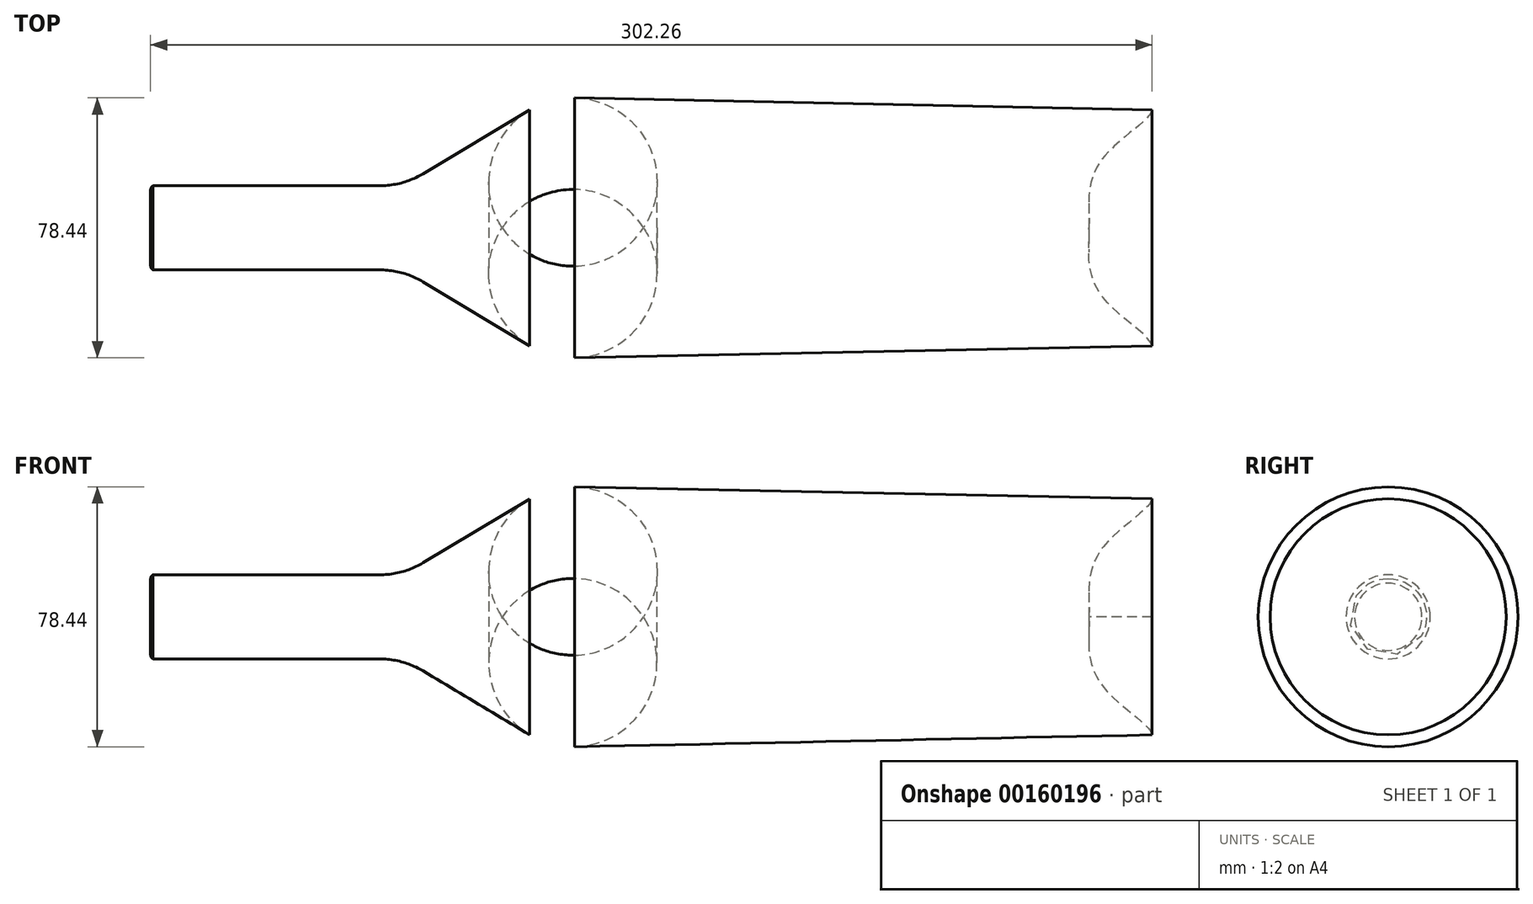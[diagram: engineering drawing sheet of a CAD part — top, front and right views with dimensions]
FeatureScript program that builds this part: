
annotation { "Feature Type Name" : "Feature", "Feature Type Description" : "" }
export const myFeature = defineFeature(function(context is Context, id is Id, definition is map)
    precondition{}
    {
        {
            var Q0;
            Q0=qCreatedBy(makeId("Top.planeOp"),FACE);
            var sketch = newSketch(context, id + "F0", { "sketchPlane" : qUnion([Q0])});
            skLineSegment(sketch, "E0", {"start": v(-285.75, -12.7) * mm, "end": v(-216.59, -12.7) * mm});
            skLineSegment(sketch, "E1", {"start": v(-203.52, -16.32) * mm, "end": v(-171.38, -35.6) * mm});
            skLineSegment(sketch, "E2", {"start": v(-157.78, -39.22) * mm, "end": v(19.05, -35.56) * mm});
            skLineSegment(sketch, "E3", {"start": v(0, 0) * mm, "end": v(-285.75, 0) * mm});
            skLineSegment(sketch, "E4", {"start": v(-285.75, 0) * mm, "end": v(-285.75, -12.7) * mm});
            skPoint(sketch, "E5.visualSharp", {"position": v(-209.55, -12.7) * mm});
            skArc(sketch, "E5.filletArc", {"start": v(-203.52, -16.32) * mm, "mid": v(-209.8, -13.62) * mm, "end": v(-216.59, -12.7) * mm});
            skPoint(sketch, "E6.visualSharp", {"position": v(-165.1, -39.37) * mm});
            skArc(sketch, "E6.filletArc", {"start": v(-171.38, -35.6) * mm, "mid": v(-164.83, -38.37) * mm, "end": v(-157.78, -39.22) * mm});
            skFitSpline(sketch, "E7", {"points": [v(19.05, -35.56) * mm, v(3.02, -18.55) * mm, v(0, -4.3) * mm, v(0, 0) * mm], "startDerivative": vector(-1.53, 31.94) * mm, "endDerivative": vector(0, 30.48) * mm});
            skFitSpline(sketch, "E8.0", {"points": [v(16.51, -35.68) * mm, v(16.5, -35.62) * mm, v(16.48, -35.41) * mm, v(16.22, -34.84) * mm, v(15.69, -34.06) * mm, v(14.9, -33.15) * mm, v(13.88, -32.16) * mm, v(12.3, -30.74) * mm, v(9.97, -28.83) * mm, v(7.45, -26.76) * mm, v(5.46, -25) * mm, v(4, -23.64) * mm, v(2.64, -22.2) * mm, v(1.6, -20.94) * mm, v(0.84, -19.87) * mm, v(0.15, -18.79) * mm, v(-0.58, -17.42) * mm, v(-1.27, -15.78) * mm, v(-1.96, -13.61) * mm, v(-2.45, -11) * mm, v(-2.61, -8.64) * mm, v(-2.63, -6.96) * mm, v(-2.6, -5.83) * mm, v(-2.57, -5) * mm, v(-2.55, -4.44) * mm, v(-2.53, -4.06) * mm, v(-2.52, -3.72) * mm, v(-2.52, -3.3) * mm, v(-2.51, -2.83) * mm, v(-2.52, -2.26) * mm, v(-2.53, -1.43) * mm, v(-2.54, -0.65) * mm, v(-2.54, 0) * mm]});
            skLineSegment(sketch, "E8.1", {"start": v(-157.84, -36.68) * mm, "end": v(14.83, -33.1) * mm});
            skLineSegment(sketch, "E8.2", {"start": v(-285.75, -10.16) * mm, "end": v(-216.59, -10.16) * mm});
            skArc(sketch, "E8.3", {"start": v(-202.21, -14.14) * mm, "mid": v(-209.13, -11.17) * mm, "end": v(-216.59, -10.16) * mm});
            skLineSegment(sketch, "E8.4", {"start": v(-202.21, -14.14) * mm, "end": v(-170.07, -33.43) * mm});
            skArc(sketch, "E8.5", {"start": v(-170.07, -33.43) * mm, "mid": v(-164.18, -35.92) * mm, "end": v(-157.84, -36.68) * mm});
            skArc(sketch, "E9", {"start": v(-285, -10.16) * mm, "mid": v(-285.75, -11.43) * mm, "end": v(-285, -12.7) * mm});
            skSolve(sketch);
        }
        {
            var Q0;
            Q0=makeQuery(id+"F0.imprint","IMPRINT",FACE,{"disambiguationData":[TD([[makeQuery(id+"F0.imprint","IMPRINT",EDGE,{"derivedFrom":sQuery(id+"F0.wireOp",EDGE,"E1")}),1.0]])]});
            var Q1;
            Q1=sQuery(id+"F0.wireOp",EDGE,"E3");
            revolve(context, id + "F1", {"entities" : qUnion([Q0]), "axis" : qUnion([Q1]), "revolveType" : RevolveType.FULL});
        }
    });
